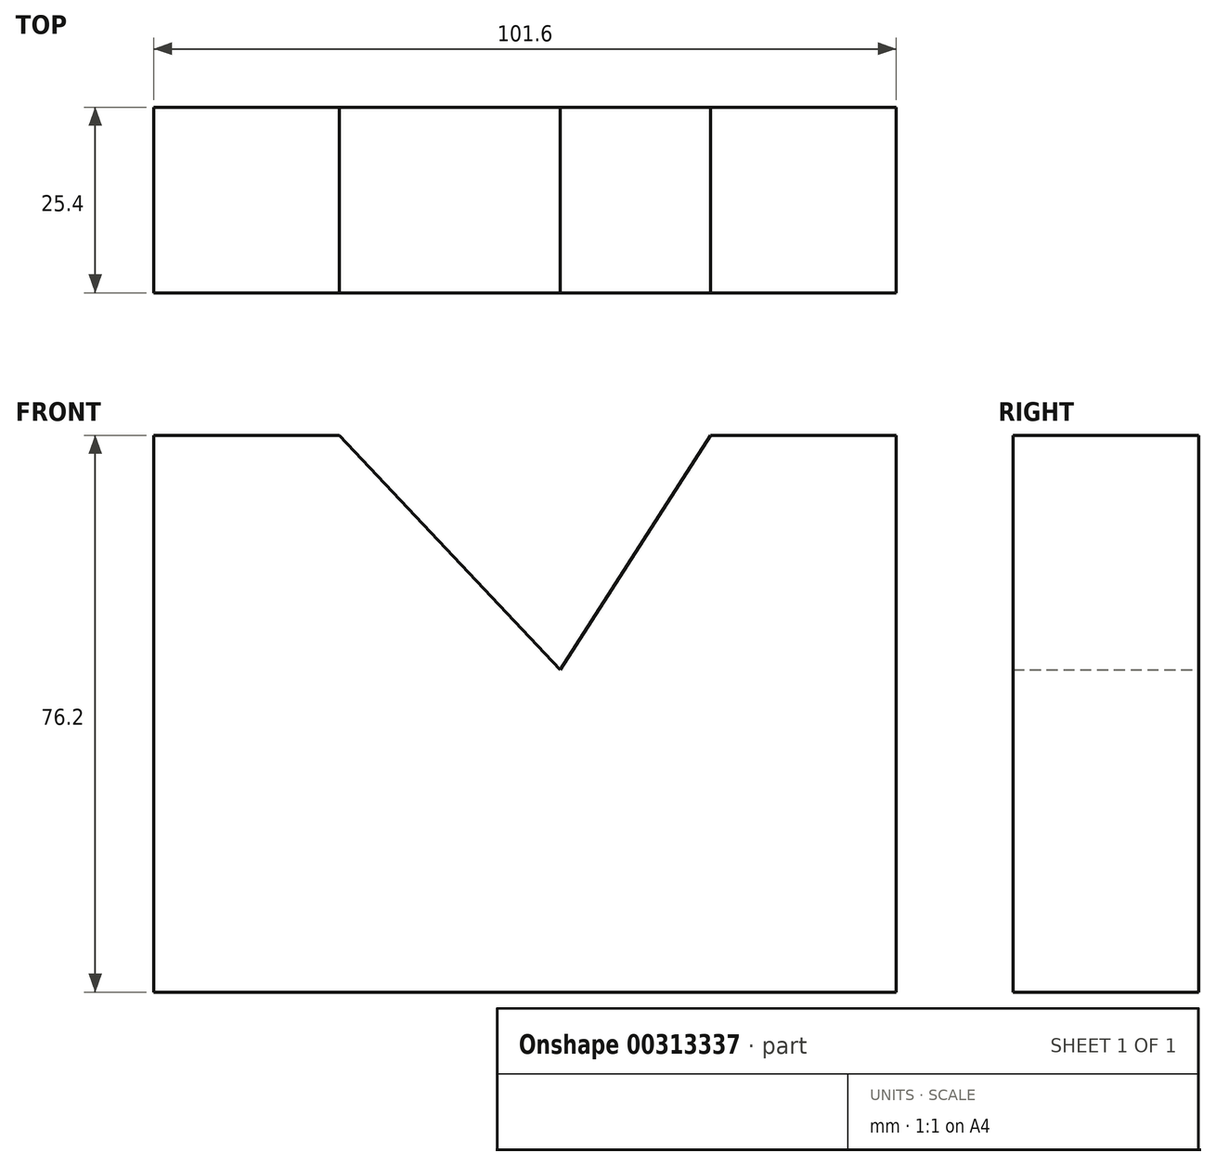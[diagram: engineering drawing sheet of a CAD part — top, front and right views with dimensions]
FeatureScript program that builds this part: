
annotation { "Feature Type Name" : "Feature", "Feature Type Description" : "" }
export const myFeature = defineFeature(function(context is Context, id is Id, definition is map)
    precondition{}
    {
        {
            var Q0;
            Q0=qCreatedBy(makeId("Front.planeOp"),FACE);
            var sketch = newSketch(context, id + "F0", { "sketchPlane" : qUnion([Q0])});
            skLineSegment(sketch, "E0", {"start": v(-61.39, -63.94) * mm, "end": v(40.21, -63.94) * mm});
            skLineSegment(sketch, "E1", {"start": v(40.21, -63.94) * mm, "end": v(40.21, 12.26) * mm});
            skLineSegment(sketch, "E2", {"start": v(-61.39, -63.94) * mm, "end": v(-61.39, 12.26) * mm});
            skLineSegment(sketch, "E3", {"start": v(-61.39, 12.26) * mm, "end": v(-35.99, 12.26) * mm});
            skLineSegment(sketch, "E4", {"start": v(40.21, 12.26) * mm, "end": v(14.81, 12.26) * mm});
            skLineSegment(sketch, "E5", {"start": v(14.81, 12.26) * mm, "end": v(-5.78, -19.8) * mm});
            skLineSegment(sketch, "E6", {"start": v(-35.99, 12.26) * mm, "end": v(-5.78, -19.8) * mm});
            skSolve(sketch);
        }
        {
            var Q0;
            Q0=makeQuery(id+"F0.imprint","IMPRINT",FACE,{"disambiguationData":[TD([[makeQuery(id+"F0.imprint","IMPRINT",EDGE,{"derivedFrom":sQuery(id+"F0.wireOp",EDGE,"E0")}),1.0]])]});
            extrude(context, id + "F1", {"entities" : qUnion([Q0]), "depth" : 25.4 * mm});
        }
    });
